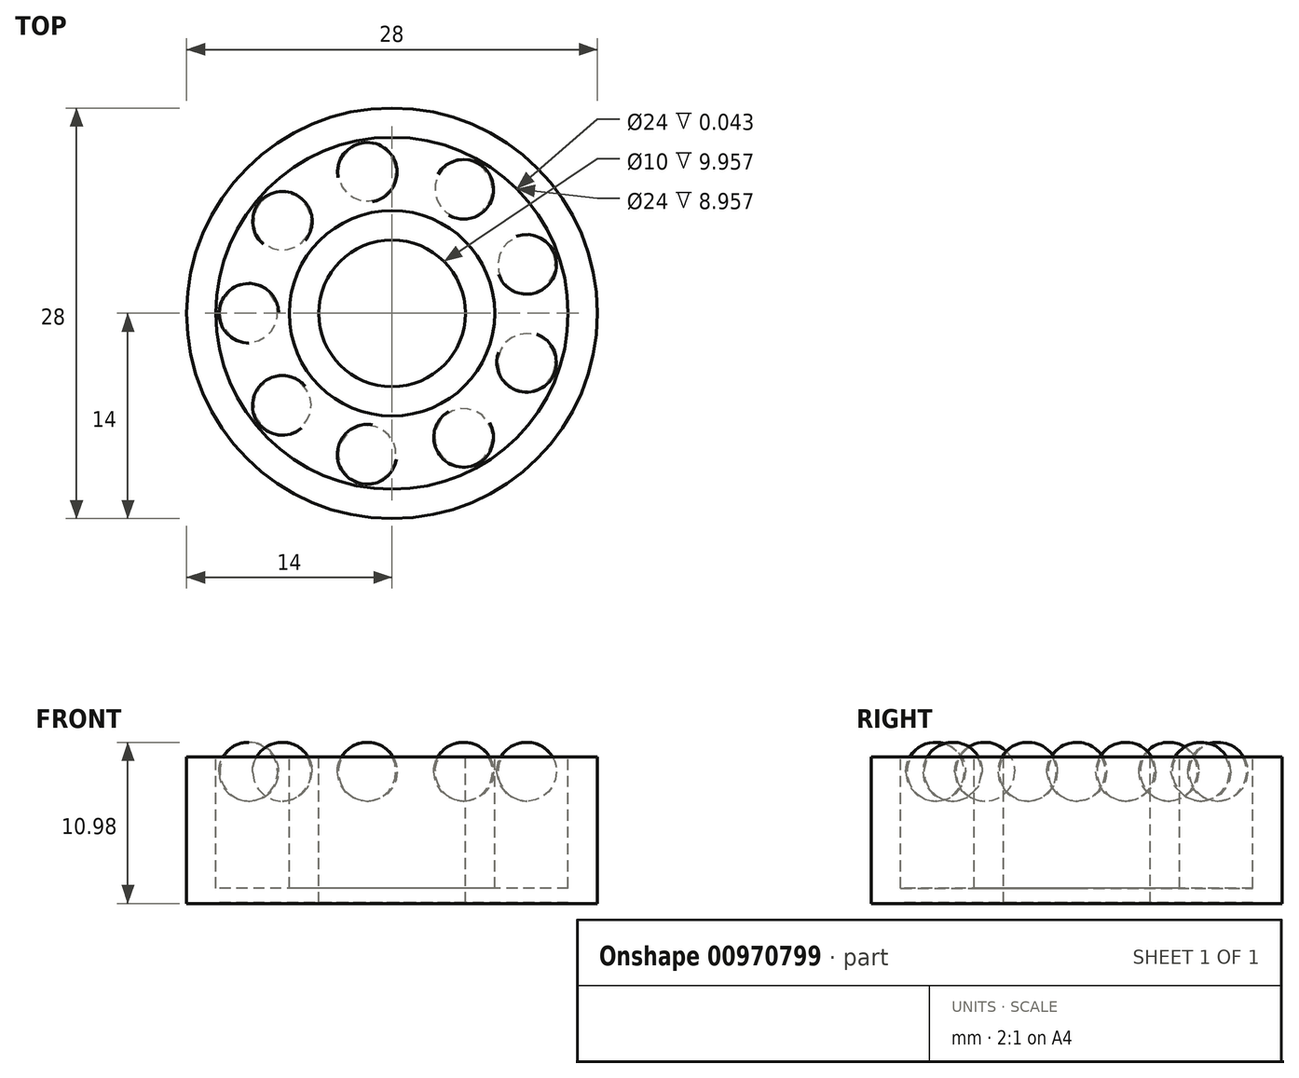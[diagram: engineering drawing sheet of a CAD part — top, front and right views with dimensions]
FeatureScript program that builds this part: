
annotation { "Feature Type Name" : "Feature", "Feature Type Description" : "" }
export const myFeature = defineFeature(function(context is Context, id is Id, definition is map)
    precondition{}
    {
        {
            var Q0;
            Q0=qCreatedBy(makeId("Front.planeOp"),FACE);
            var sketch = newSketch(context, id + "F0", { "sketchPlane" : qUnion([Q0])});
            skLineSegment(sketch, "E0.bottom", {"start": v(-14, 8.96) * mm, "end": v(-12, 8.96) * mm});
            skLineSegment(sketch, "E0.top", {"start": v(-14, -1.04) * mm, "end": v(-12, -1.04) * mm});
            skLineSegment(sketch, "E0.left", {"start": v(-14, 8.96) * mm, "end": v(-14, -1.04) * mm});
            skLineSegment(sketch, "E0.right", {"start": v(-12, 8.96) * mm, "end": v(-12, -1.04) * mm});
            skLineSegment(sketch, "E1.bottom", {"start": v(-12, -1) * mm, "end": v(-5, -1) * mm});
            skLineSegment(sketch, "E1.top", {"start": v(-12, 0) * mm, "end": v(-5, 0) * mm});
            skLineSegment(sketch, "E1.left", {"start": v(-12, -1) * mm, "end": v(-12, 0) * mm});
            skLineSegment(sketch, "E1.right", {"start": v(-5, -1) * mm, "end": v(-5, 0) * mm});
            skLineSegment(sketch, "E2.bottom", {"start": v(-5, 0) * mm, "end": v(-7, 0) * mm});
            skLineSegment(sketch, "E2.top", {"start": v(-5, 8.96) * mm, "end": v(-7, 8.96) * mm});
            skLineSegment(sketch, "E2.left", {"start": v(-5, 0) * mm, "end": v(-5, 8.96) * mm});
            skLineSegment(sketch, "E2.right", {"start": v(-7, 0) * mm, "end": v(-7, 8.96) * mm});
            skLineSegment(sketch, "E3", {"start": v(0, 43.48) * mm, "end": v(0, -41.5) * mm});
            skSolve(sketch);
        }
        {
            var Q0;
            Q0=qSketchRegion(id+"F0",true);
            var Q1;
            Q1=sQuery(id+"F0.wireOp",EDGE,"E3");
            revolve(context, id + "F1", {"surfaceOperationType" : NewSurfaceOperationType.NEW, "entities" : qUnion([Q0]), "axis" : qUnion([Q1]), "revolveType" : RevolveType.FULL});
        }
        {
            var Q0;
            Q0=qCreatedBy(makeId("Front.planeOp"),FACE);
            var sketch = newSketch(context, id + "F2", { "sketchPlane" : qUnion([Q0])});
            skArc(sketch, "E4", {"start": v(-9.78, 9.94) * mm, "mid": v(-11.8, 7.92) * mm, "end": v(-9.75, 5.94) * mm});
            skLineSegment(sketch, "E5", {"start": v(-9.78, 9.94) * mm, "end": v(-9.75, 5.94) * mm});
            skSolve(sketch);
        }
        {
            var Q0;
            Q0=qSketchRegion(id+"F2",true);
            var Q1;
            Q1=sQuery(id+"F2.wireOp",EDGE,"E5");
            revolve(context, id + "F3", {"surfaceOperationType" : NewSurfaceOperationType.NEW, "entities" : qUnion([Q0]), "axis" : qUnion([Q1]), "revolveType" : RevolveType.FULL});
        }
        {
            var Q0;
            Q0=makeQuery(id+"F3.opRevolve","SWEPT_BODY",BODY,{"disambiguationData":[OSD([sQuery(id+"F2.wireOp",EDGE,"E4"),sQuery(id+"F2.wireOp",EDGE,"E5")])]});
            var Q1;
            Q1=makeQuery(id+"F1.opRevolve","SWEPT_EDGE",EDGE,{"disambiguationData":[OSD([sQuery(id+"F0.wireOp",EDGE,"E0.bottom"),sQuery(id+"F0.wireOp",EDGE,"E0.right")])]});
            circularPattern(context, id + "F4", {"entities" : qUnion([Q0]), "axis" : qUnion([Q1]), "angle" : 360 * degree, "instanceCount" : 9, "equalSpace" : true});
        }
    });
